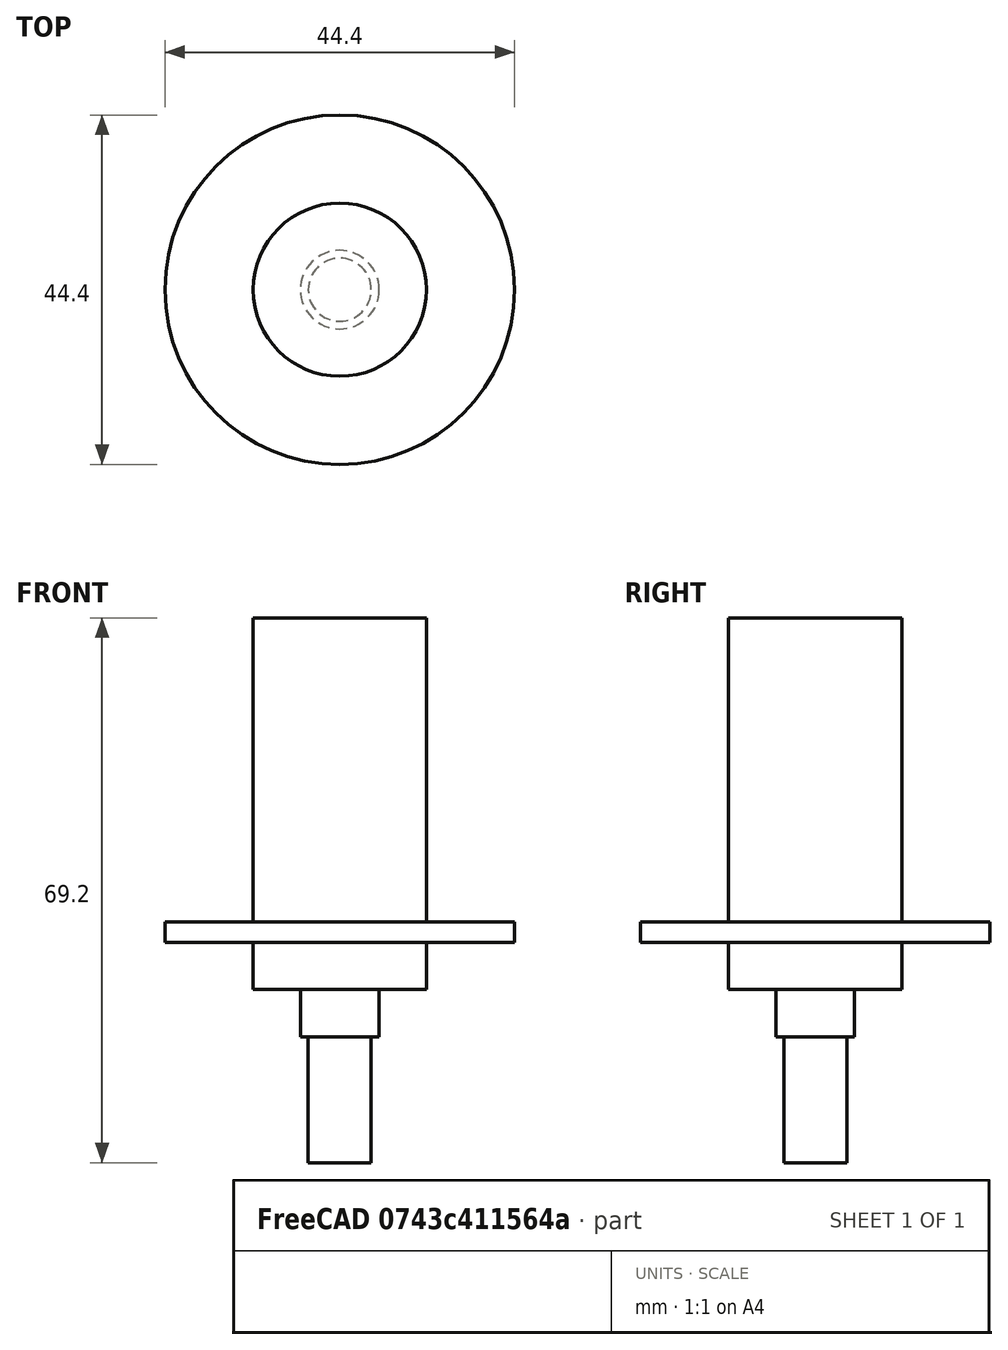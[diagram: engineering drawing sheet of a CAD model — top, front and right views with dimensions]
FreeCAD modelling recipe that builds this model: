
FCSTD DOCUMENT  (FreeCAD 0.20R29177 +426 (Git))
Label: SlipRing
License: All rights reserved
LicenseURL: http://en.wikipedia.org/wiki/All_rights_reserved
objects: App::DocumentObjectGroup×3, PartDesign::CoordinateSystem×1, App::FeaturePython×1, Sketcher::SketchObject×1, PartDesign::Revolution×1, PartDesign::Body×1, App::Part×1
note: 5 computed .brp shape members not serialized (recipe doc carries the construction recipe); baked Part::Feature solids carry a one-line shape summary decoded from their .brp

FEATURE [App::DocumentObjectGroup] Parts
FEATURE [PartDesign::CoordinateSystem] LCS_Origin
  AttacherType = Attacher::AttachEngine3D
  MapMode = 2
  Support = -> [X_Axis]
FEATURE [App::FeaturePython] Variables  # WARN: FeaturePython — macro-defined, semantics opaque (R4)
  Type = App::PropertyContainer
FEATURE [App::DocumentObjectGroup] Constraints
FEATURE [App::DocumentObjectGroup] Configurations
FEATURE [Sketcher::SketchObject] Sketch
  FullyConstrained = true
  MapMode = 5
  Placement = pos=(0,0,0) rot=(1,0,0;1.5708rad)
  Support = -> [XZ_Plane001]
  sketch-geometry (14):
    g0: LineSegment StartX=0 StartY=38.6 StartZ=0 EndX=11 EndY=38.6 EndZ=0
    g1: LineSegment StartX=11 StartY=38.6 StartZ=0 EndX=11 EndY=0 EndZ=0
    g2: LineSegment StartX=11 StartY=0 StartZ=0 EndX=22.2 EndY=0 EndZ=0
    g3: LineSegment StartX=22.2 StartY=0 StartZ=0 EndX=22.2 EndY=-2.6 EndZ=0
    g4: LineSegment StartX=22.2 StartY=-2.6 StartZ=0 EndX=11 EndY=-2.6 EndZ=0
    g5: LineSegment StartX=11 StartY=-2.6 StartZ=0 EndX=11 EndY=-8.6 EndZ=0
    g6: LineSegment StartX=11 StartY=-8.6 StartZ=0 EndX=5 EndY=-8.6 EndZ=0
    g7: LineSegment StartX=5 StartY=-8.6 StartZ=0 EndX=5 EndY=-14.6 EndZ=0
    g8: LineSegment StartX=0 StartY=-14.6 StartZ=0 EndX=0 EndY=38.6 EndZ=0
    g9: LineSegment StartX=5 StartY=-14.6 StartZ=0 EndX=4 EndY=-14.6 EndZ=0
    g10: LineSegment StartX=4 StartY=-14.6 StartZ=0 EndX=0 EndY=-14.6 EndZ=0
    g11: LineSegment StartX=4 StartY=-14.6 StartZ=0 EndX=4 EndY=-30.6 EndZ=0
    g12: LineSegment StartX=4 StartY=-30.6 StartZ=0 EndX=0 EndY=-30.6 EndZ=0
    g13: LineSegment StartX=0 StartY=-30.6 StartZ=0 EndX=0 EndY=-14.6 EndZ=0
  constraints (41):
    c: PointOnObject(g0,g-2)
    c: Horizontal(g0)
    c: Coincident(g0,g1)
    c: Vertical(g1)
    c: Coincident(g1,g2)
    c: Horizontal(g2)
    c: Coincident(g2,g3)
    c: Vertical(g3)
    c: Coincident(g3,g4)
    c: Horizontal(g4)
    c: Coincident(g4,g5)
    c: Vertical(g5)
    c: Coincident(g5,g6)
    c: Coincident(g6,g7)
    c: Vertical(g7)
    c: Coincident(g7,g9)
    c: PointOnObject(g10,g-2)
    c: Coincident(g10,g8)
    c: Coincident(g8,g0)
    c: Horizontal(g6)
    c: DistanceX(g0,g0) = 11
    c: DistanceX(g-1,g3) = 22.2
    c: PointOnObject(g1,g5)
    c: DistanceX(g10,g9) = 5
    c: DistanceY(g7,g7) = 6
    c: DistanceY(g5,g5) = 6
    c: DistanceY(g3,g3) = 2.6
    c: DistanceY(g1,g1) = 38.6
    c: PointOnObject(g1,g-1)
    c: Coincident(g9,g10)
    c: Horizontal(g9)
    c: Horizontal(g10)
    c: Coincident(g11,g9)
    c: Vertical(g11)
    c: Coincident(g12,g11)
    c: PointOnObject(g12,g-2)
    c: Horizontal(g12)
    c: Coincident(g13,g12)
    c: Coincident(g13,g8)
    c: DistanceX(g12,g12) = 4
    c: DistanceY(g13,g13) = 16
FEATURE [PartDesign::Revolution] Revolution
  Angle = 360
  Axis = (0,-2e-16,1)
  Base = (0,0,0)
  Placement = pos=(0,0,0) rot=(1,0,0;1.5708rad)
  Profile = -> Sketch
  ReferenceAxis = -> Sketch [V_Axis]
  Reversed = true
FEATURE [PartDesign::Body] Body
  Group = -> [Sketch,Revolution]
  Origin = -> Origin001
  Tip = -> Revolution
FEATURE [App::Part] Assembly
  AssemblyType = Part::Link
  Group = -> [LCS_Origin,Variables,Constraints,Configurations,Body]
  Origin = -> Origin
  Type = Assembly
